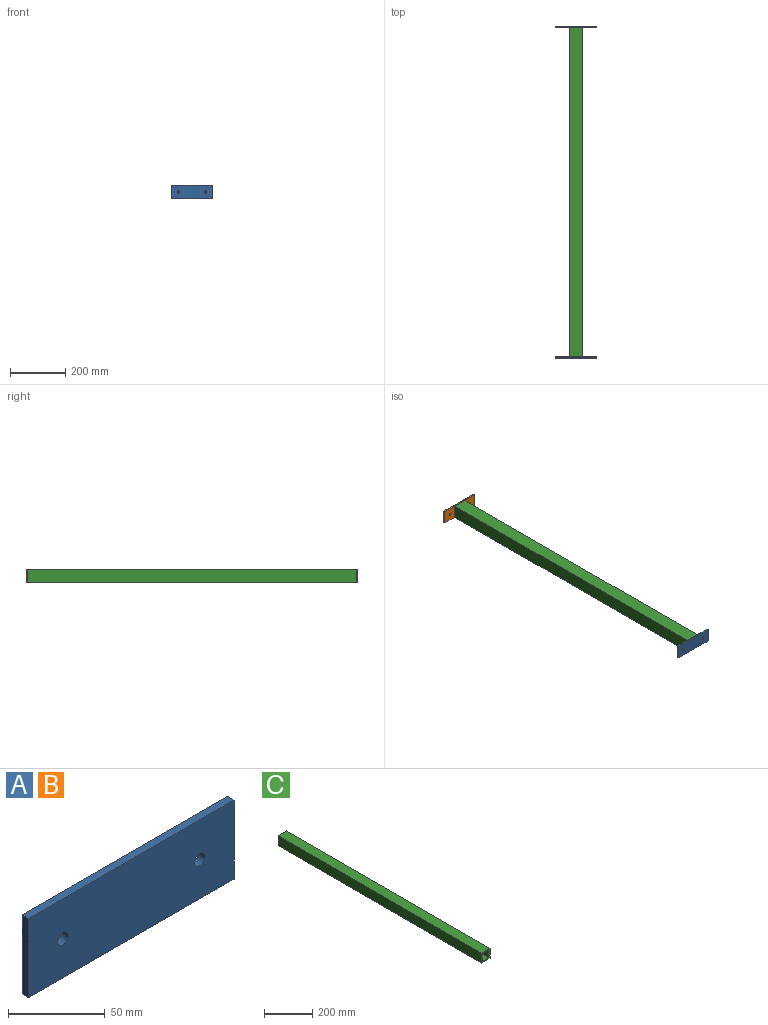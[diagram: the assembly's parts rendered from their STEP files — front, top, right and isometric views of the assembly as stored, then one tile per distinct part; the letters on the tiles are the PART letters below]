
ASSEMBLY  parts=3 mates=2
PART A: 8 faces, bbox 150x5x50 mm
  f0: plane 50x5mm, normal (-1,0,0), area 250mm2, adj f1,f3,f4,f5
  f1: plane 150x5mm, normal (0,0,-1), area 750mm2, adj f0,f2,f4,f5
  f2: plane 50x5mm, normal (1,0,0), area 250mm2, adj f1,f3,f4,f5
  f3: plane 150x5mm, normal (0,0,1), area 750mm2, adj f0,f2,f4,f5
  f4: plane 150x50mm, normal (0,-1,0), area 7399.5mm2, adj f0,f1,f2,f3,f6,f7
  f5: plane 150x50mm, normal (0,1,0), area 7399.5mm2, adj f0,f1,f2,f3,f6,f7
  f6: cylinder r=4mm len=8mm, axis (0,-1,0), area 125.7mm2, adj f4,f5
  f7: cylinder r=4mm len=8mm, axis (0,-1,0), area 125.7mm2, adj f4,f5
PART B: same geometry as A
PART C: 10 faces, bbox 50x1190x50 mm
  f0: plane 1190x38mm, normal (1,0,0), area 45220mm2, adj f1,f7,f8,f9
  f1: plane 1190x38mm, normal (0,0,-1), area 45220mm2, adj f0,f2,f8,f9
  f2: plane 1190x38mm, normal (-1,0,0), area 45220mm2, adj f1,f7,f8,f9
  f3: plane 1190x50mm, normal (-1,0,0), area 59500mm2, adj f4,f6,f8,f9
  f4: plane 1190x50mm, normal (0,0,-1), area 59500mm2, adj f3,f5,f8,f9
  f5: plane 1190x50mm, normal (1,0,0), area 59500mm2, adj f4,f6,f8,f9
  f6: plane 1190x50mm, normal (0,0,1), area 59500mm2, adj f3,f5,f8,f9
  f7: plane 1190x38mm, normal (0,0,1), area 45220mm2, adj f0,f2,f8,f9
  f8: plane 50x50mm, normal (0,-1,0), area 1056mm2, adj f0,f1,f2,f3,f4,f5,f6,f7
  f9: plane 50x50mm, normal (0,1,0), area 1056mm2, adj f0,f1,f2,f3,f4,f5,f6,f7
PLACE A t=(-546.79,-371.89,-193)mm
PLACE B t=(-546.79,823.11,-193)mm
PLACE C t=(-496.79,818.11,-193)mm
MATE fastened C.f8 <-> A.f5  axis (0,-1,0) through (-471.79,-371.89,-168)mm
MATE fastened B.f4 <-> C.f9  axis (0,-1,0) through (-471.79,818.11,-168)mm
